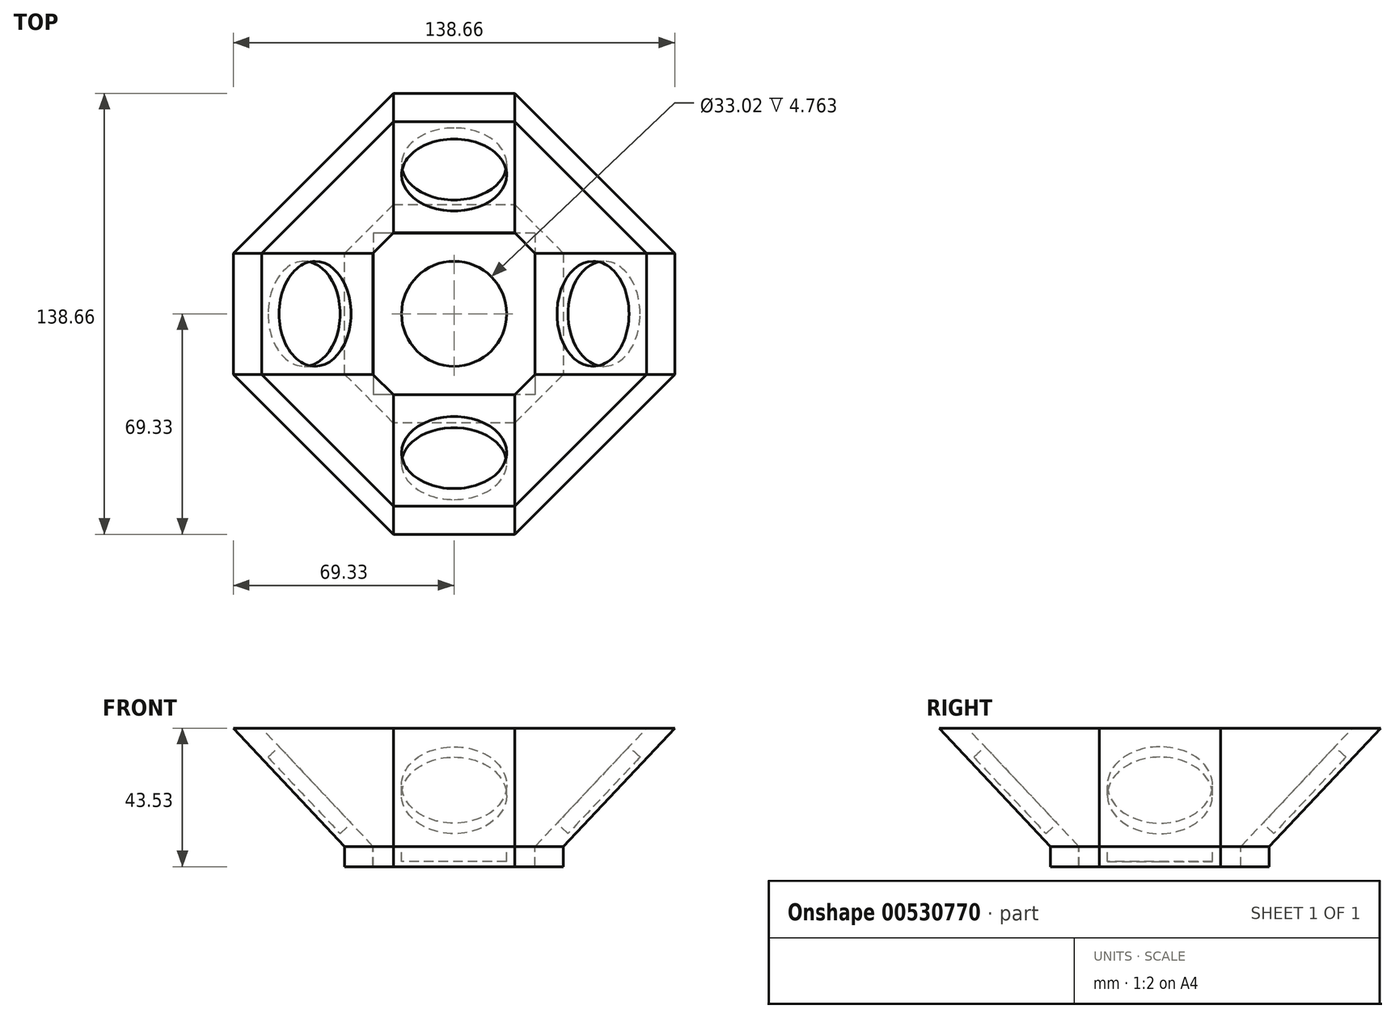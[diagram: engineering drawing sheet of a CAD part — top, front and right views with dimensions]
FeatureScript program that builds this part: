
annotation { "Feature Type Name" : "Feature", "Feature Type Description" : "" }
export const myFeature = defineFeature(function(context is Context, id is Id, definition is map)
    precondition{}
    {
        {
            var Q0;
            Q0=qCreatedBy(makeId("Top.planeOp"),FACE);
            var sketch = newSketch(context, id + "F0", { "sketchPlane" : qUnion([Q0])});
            skLineSegment(sketch, "E0.bottom", {"start": v(25.4, 25.4) * mm, "end": v(-25.4, 25.4) * mm});
            skLineSegment(sketch, "E0.top", {"start": v(25.4, -25.4) * mm, "end": v(-25.4, -25.4) * mm});
            skLineSegment(sketch, "E0.left", {"start": v(25.4, 25.4) * mm, "end": v(25.4, -25.4) * mm});
            skLineSegment(sketch, "E0.right", {"start": v(-25.4, 25.4) * mm, "end": v(-25.4, -25.4) * mm});
            skPoint(sketch, "E0.middle", {"position": v(0, 0) * mm});
            skSolve(sketch);
        }
        {
            var Q0;
            Q0=qCreatedBy(makeId("Right.planeOp"),FACE);
            var sketch = newSketch(context, id + "F1", { "sketchPlane" : qUnion([Q0])});
            skLineSegment(sketch, "E1", {"start": v(-25.47, 0) * mm, "end": v(-60.44, 37.18) * mm});
            skLineSegment(sketch, "E2", {"start": v(-60.44, 37.18) * mm, "end": v(-69.33, 37.18) * mm});
            skLineSegment(sketch, "E3", {"start": v(-69.33, 37.18) * mm, "end": v(-34.36, 0) * mm});
            skLineSegment(sketch, "E4", {"start": v(-34.36, 0) * mm, "end": v(-25.47, 0) * mm});
            skSolve(sketch);
        }
        {
            var Q0;
            Q0 = qSketchRegion(id + "F1", true);
            extrude(context, id + "F2", {"entities" : qUnion([Q0]), "depth" : 19.05 * mm, "offsetDistance" : 25.4 * mm});
        }
        {
            var Q0;
            Q0=makeQuery(id+"F2.opExtrude","CAP_FACE",FACE,{"disambiguationData":[OSD([sQuery(id+"F1.wireOp",EDGE,"E1"),sQuery(id+"F1.wireOp",EDGE,"E2"),sQuery(id+"F1.wireOp",EDGE,"E3"),sQuery(id+"F1.wireOp",EDGE,"E4")])],"isStart":true});
            extrude(context, id + "F3", {"entities" : qUnion([Q0]), "operationType" : NewBodyOperationType.ADD, "depth" : 19.05 * mm, "offsetDistance" : 25.4 * mm});
        }
        {
            var Q0;
            {var subQ0=sQuery(id+"F1.wireOp",EDGE,"E1");Q0=makeQuery(id+"F3.boolean.opBoolean","MERGE",FACE,{"derivedFrom":[makeQuery(id+"F2.opExtrude","SWEPT_FACE",FACE,{"disambiguationData":[OSD([subQ0])]}),makeQuery(id+"F3.opExtrude","SWEPT_FACE",FACE,{"disambiguationData":[OSD([subQ0])]})]});}
            var sketch = newSketch(context, id + "F4", { "sketchPlane" : qUnion([Q0])});
            skCircle(sketch, "E5", {"center": v(0, 43.98) * mm, "radius": 16.51 * mm});
            skSolve(sketch);
        }
        {
            var Q0;
            Q0 = qSketchRegion(id + "F4", true);
            extrude(context, id + "F5", {"entities" : qUnion([Q0]), "operationType" : NewBodyOperationType.REMOVE, "oppositeDirection" : true, "depth" : 4.76 * mm, "offsetDistance" : 25.4 * mm});
        }
        {
            var Q0;
            Q0=makeQuery(id+"F0.imprint","IMPRINT",FACE,{"disambiguationData":[TD([[makeQuery(id+"F0.imprint","IMPRINT",EDGE,{"derivedFrom":sQuery(id+"F0.wireOp",EDGE,"E0.bottom")}),1.0]])]});
            var sketch = newSketch(context, id + "F6", { "sketchPlane" : qUnion([Q0])});
            skCircle(sketch, "E6", {"center": v(0, 0) * mm, "radius": 16.51 * mm});
            skSolve(sketch);
        }
        {
            var Q0;
            Q0=makeQuery(id+"F2.opExtrude","SWEPT_BODY",BODY,{"disambiguationData":[OSD([sQuery(id+"F1.wireOp",EDGE,"E1"),sQuery(id+"F1.wireOp",EDGE,"E2"),sQuery(id+"F1.wireOp",EDGE,"E3"),sQuery(id+"F1.wireOp",EDGE,"E4")])]});
            var Q1;
            Q1=sQuery(id+"F6.wireOp",EDGE,"E6");
            circularPattern(context, id + "F7", {"entities" : qUnion([Q0]), "axis" : qUnion([Q1]), "angle" : 360 * degree, "instanceCount" : 4, "equalSpace" : true});
        }
        {
            var Q0;
            Q0=makeQuery(id+"F2.opExtrude","CAP_FACE",FACE,{"disambiguationData":[OSD([sQuery(id+"F1.wireOp",EDGE,"E1"),sQuery(id+"F1.wireOp",EDGE,"E2"),sQuery(id+"F1.wireOp",EDGE,"E3"),sQuery(id+"F1.wireOp",EDGE,"E4")])],"isStart":false});
            var Q1;
            Q1=makeQuery(id+"F7.opPattern","COPY",FACE,{"derivedFrom":makeQuery(id+"F3.opExtrude","CAP_FACE",FACE,{"disambiguationData":[OSD([sQuery(id+"F1.wireOp",EDGE,"E1"),sQuery(id+"F1.wireOp",EDGE,"E2"),sQuery(id+"F1.wireOp",EDGE,"E3"),sQuery(id+"F1.wireOp",EDGE,"E4")])],"isStart":false}),"instanceName":"1"});
            loft(context, id + "F8", {"sheetProfilesArray" : [{ "sheetProfileEntities" : qUnion([Q0]) }, { "sheetProfileEntities" : qUnion([Q1]) }]});
        }
        {
            var Q0;
            Q0=makeQuery(id+"F7.opPattern","COPY",FACE,{"derivedFrom":makeQuery(id+"F2.opExtrude","CAP_FACE",FACE,{"disambiguationData":[OSD([sQuery(id+"F1.wireOp",EDGE,"E1"),sQuery(id+"F1.wireOp",EDGE,"E2"),sQuery(id+"F1.wireOp",EDGE,"E3"),sQuery(id+"F1.wireOp",EDGE,"E4")])],"isStart":false}),"instanceName":"1"});
            var Q1;
            Q1=makeQuery(id+"F7.opPattern","COPY",FACE,{"derivedFrom":makeQuery(id+"F3.opExtrude","CAP_FACE",FACE,{"disambiguationData":[OSD([sQuery(id+"F1.wireOp",EDGE,"E1"),sQuery(id+"F1.wireOp",EDGE,"E2"),sQuery(id+"F1.wireOp",EDGE,"E3"),sQuery(id+"F1.wireOp",EDGE,"E4")])],"isStart":false}),"instanceName":"2"});
            loft(context, id + "F9", {"sheetProfilesArray" : [{ "sheetProfileEntities" : qUnion([Q0]) }, { "sheetProfileEntities" : qUnion([Q1]) }]});
        }
        {
            var Q0;
            Q0=makeQuery(id+"F7.opPattern","COPY",FACE,{"derivedFrom":makeQuery(id+"F2.opExtrude","CAP_FACE",FACE,{"disambiguationData":[OSD([sQuery(id+"F1.wireOp",EDGE,"E1"),sQuery(id+"F1.wireOp",EDGE,"E2"),sQuery(id+"F1.wireOp",EDGE,"E3"),sQuery(id+"F1.wireOp",EDGE,"E4")])],"isStart":false}),"instanceName":"2"});
            var Q1;
            Q1=makeQuery(id+"F7.opPattern","COPY",FACE,{"derivedFrom":makeQuery(id+"F3.opExtrude","CAP_FACE",FACE,{"disambiguationData":[OSD([sQuery(id+"F1.wireOp",EDGE,"E1"),sQuery(id+"F1.wireOp",EDGE,"E2"),sQuery(id+"F1.wireOp",EDGE,"E3"),sQuery(id+"F1.wireOp",EDGE,"E4")])],"isStart":false}),"instanceName":"3"});
            loft(context, id + "F10", {"sheetProfilesArray" : [{ "sheetProfileEntities" : qUnion([Q0]) }, { "sheetProfileEntities" : qUnion([Q1]) }]});
        }
        {
            var Q0;
            Q0=makeQuery(id+"F7.opPattern","COPY",FACE,{"derivedFrom":makeQuery(id+"F2.opExtrude","CAP_FACE",FACE,{"disambiguationData":[OSD([sQuery(id+"F1.wireOp",EDGE,"E1"),sQuery(id+"F1.wireOp",EDGE,"E2"),sQuery(id+"F1.wireOp",EDGE,"E3"),sQuery(id+"F1.wireOp",EDGE,"E4")])],"isStart":false}),"instanceName":"3"});
            var Q1;
            Q1=makeQuery(id+"F3.opExtrude","CAP_FACE",FACE,{"disambiguationData":[OSD([sQuery(id+"F1.wireOp",EDGE,"E1"),sQuery(id+"F1.wireOp",EDGE,"E2"),sQuery(id+"F1.wireOp",EDGE,"E3"),sQuery(id+"F1.wireOp",EDGE,"E4")])],"isStart":false});
            loft(context, id + "F11", {"sheetProfilesArray" : [{ "sheetProfileEntities" : qUnion([Q0]) }, { "sheetProfileEntities" : qUnion([Q1]) }]});
        }
        {
            var Q0;
            Q0=makeQuery(id+"F0.imprint","IMPRINT",FACE,{"disambiguationData":[TD([[makeQuery(id+"F0.imprint","IMPRINT",EDGE,{"derivedFrom":sQuery(id+"F0.wireOp",EDGE,"E0.bottom")}),1.0]])]});
            extrude(context, id + "F12", {"entities" : qUnion([Q0]), "oppositeDirection" : true, "depth" : 6.35 * mm, "offsetDistance" : 25.4 * mm});
        }
        {
            var Q0;
            {var subQ0=sQuery(id+"F1.wireOp",EDGE,"E4");Q0=makeQuery(id+"F7.opPattern","COPY",FACE,{"derivedFrom":makeQuery(id+"F3.boolean.opBoolean","MERGE",FACE,{"derivedFrom":[makeQuery(id+"F2.opExtrude","SWEPT_FACE",FACE,{"disambiguationData":[OSD([subQ0])]}),makeQuery(id+"F3.opExtrude","SWEPT_FACE",FACE,{"disambiguationData":[OSD([subQ0])]})]}),"instanceName":"1"});}
            var Q1;
            Q1=makeQuery(id+"F9.opLoft","SWEPT_FACE",FACE,{"disambiguationData":[OSD([sQuery(id+"F1.wireOp",EDGE,"E1"),sQuery(id+"F1.wireOp",EDGE,"E3"),sQuery(id+"F1.wireOp",EDGE,"E4")])]});
            var Q2;
            {var subQ0=sQuery(id+"F1.wireOp",EDGE,"E4");Q2=makeQuery(id+"F7.opPattern","COPY",FACE,{"derivedFrom":makeQuery(id+"F3.boolean.opBoolean","MERGE",FACE,{"derivedFrom":[makeQuery(id+"F2.opExtrude","SWEPT_FACE",FACE,{"disambiguationData":[OSD([subQ0])]}),makeQuery(id+"F3.opExtrude","SWEPT_FACE",FACE,{"disambiguationData":[OSD([subQ0])]})]}),"instanceName":"2"});}
            var Q3;
            {var subQ0=sQuery(id+"F1.wireOp",EDGE,"E4");Q3=makeQuery(id+"F7.opPattern","COPY",FACE,{"derivedFrom":makeQuery(id+"F3.boolean.opBoolean","MERGE",FACE,{"derivedFrom":[makeQuery(id+"F2.opExtrude","SWEPT_FACE",FACE,{"disambiguationData":[OSD([subQ0])]}),makeQuery(id+"F3.opExtrude","SWEPT_FACE",FACE,{"disambiguationData":[OSD([subQ0])]})]}),"instanceName":"3"});}
            var Q4;
            Q4=makeQuery(id+"F10.opLoft","SWEPT_FACE",FACE,{"disambiguationData":[OSD([sQuery(id+"F1.wireOp",EDGE,"E1"),sQuery(id+"F1.wireOp",EDGE,"E3"),sQuery(id+"F1.wireOp",EDGE,"E4")])]});
            var Q5;
            Q5=makeQuery(id+"F11.opLoft","SWEPT_FACE",FACE,{"disambiguationData":[OSD([sQuery(id+"F1.wireOp",EDGE,"E1"),sQuery(id+"F1.wireOp",EDGE,"E3"),sQuery(id+"F1.wireOp",EDGE,"E4")])]});
            var Q6;
            {var subQ0=sQuery(id+"F1.wireOp",EDGE,"E4");Q6=makeQuery(id+"F3.boolean.opBoolean","MERGE",FACE,{"derivedFrom":[makeQuery(id+"F2.opExtrude","SWEPT_FACE",FACE,{"disambiguationData":[OSD([subQ0])]}),makeQuery(id+"F3.opExtrude","SWEPT_FACE",FACE,{"disambiguationData":[OSD([subQ0])]})]});}
            var Q7;
            Q7=makeQuery(id+"F8.opLoft","SWEPT_FACE",FACE,{"disambiguationData":[OSD([sQuery(id+"F1.wireOp",EDGE,"E1"),sQuery(id+"F1.wireOp",EDGE,"E3"),sQuery(id+"F1.wireOp",EDGE,"E4")])]});
            extrude(context, id + "F13", {"entities" : qUnion([Q0, Q1, Q2, Q3, Q4, Q5, Q6, Q7]), "depth" : 6.35 * mm, "offsetDistance" : 25.4 * mm});
        }
        {
            var Q0;
            Q0=makeQuery(id+"F12.opExtrude","CAP_FACE",FACE,{"disambiguationData":[OSD([sQuery(id+"F0.wireOp",EDGE,"E0.bottom"),sQuery(id+"F0.wireOp",EDGE,"E0.top"),sQuery(id+"F0.wireOp",EDGE,"E0.left"),sQuery(id+"F0.wireOp",EDGE,"E0.right")])],"isStart":true});
            var sketch = newSketch(context, id + "F14", { "sketchPlane" : qUnion([Q0])});
            skCircle(sketch, "E7", {"center": v(0, 0) * mm, "radius": 16.51 * mm});
            skSolve(sketch);
        }
        {
            var Q0;
            Q0=makeQuery(id+"F14.imprint","IMPRINT",FACE,{"disambiguationData":[TD([[makeQuery(id+"F14.imprint","IMPRINT",EDGE,{"derivedFrom":sQuery(id+"F14.wireOp",EDGE,"E7")}),1.0]])]});
            extrude(context, id + "F15", {"entities" : qUnion([Q0]), "operationType" : NewBodyOperationType.REMOVE, "oppositeDirection" : true, "depth" : 4.76 * mm, "offsetDistance" : 25.4 * mm});
        }
    });
